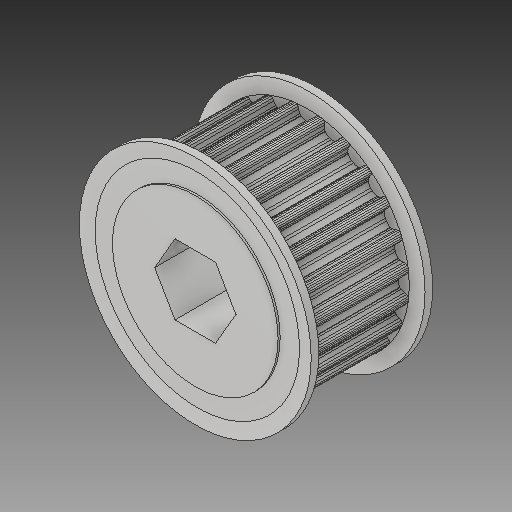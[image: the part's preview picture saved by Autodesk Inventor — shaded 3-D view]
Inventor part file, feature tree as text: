
AUTODESK INVENTOR PART (.ipt)
format: ipt  version: 2018 (Build 220112000, 112)  size: 710,144 bytes
history: native  units: in
note: dims shown in document units (in); Inventor stores cm internally (conversion verified against a paired STEP export)
features: mirror x1
ambient origin geometry x8: Origin, YZ Plane, XZ Plane, XY Plane, X Axis, Y Axis, Z Axis, Center Point
bodies: Solid1 (feature_tree)
feature tree (1):
  mirror  "Mirror1"
